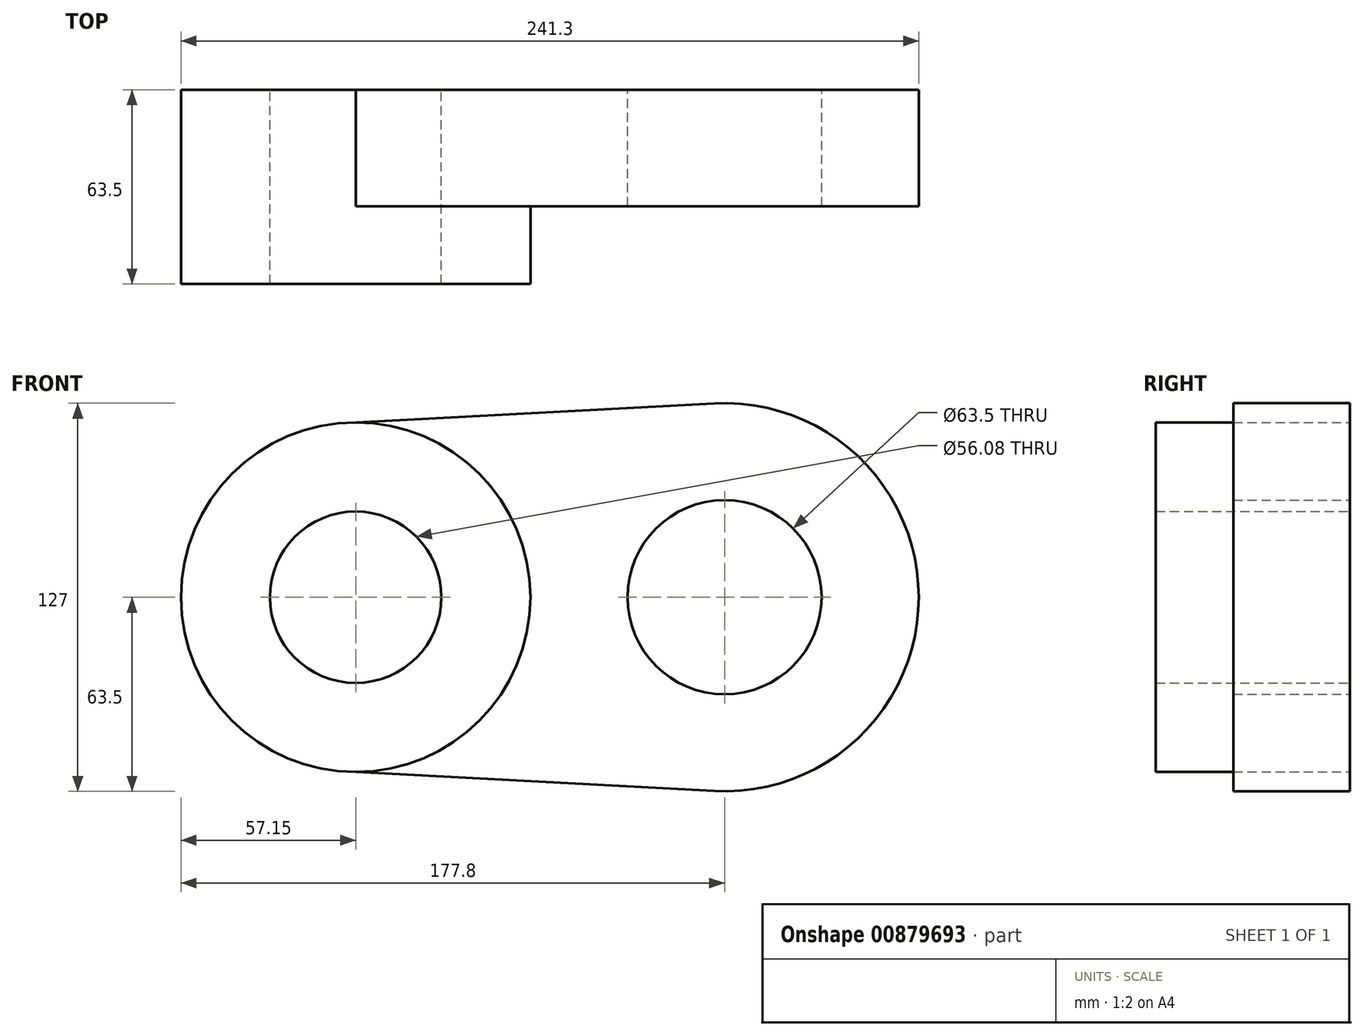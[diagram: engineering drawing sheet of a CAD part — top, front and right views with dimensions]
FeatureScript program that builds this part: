
annotation { "Feature Type Name" : "Feature", "Feature Type Description" : "" }
export const myFeature = defineFeature(function(context is Context, id is Id, definition is map)
    precondition{}
    {
        {
            var Q0;
            Q0=qCreatedBy(makeId("Front.planeOp"),FACE);
            var sketch = newSketch(context, id + "F0", { "sketchPlane" : qUnion([Q0])});
            skCircle(sketch, "E0", {"center": v(0, 0) * mm, "radius": 57.15 * mm});
            skCircle(sketch, "E1", {"center": v(120.65, 0) * mm, "radius": 63.5 * mm});
            skLineSegment(sketch, "E2", {"start": v(0, 57.15) * mm, "end": v(117.27, 63.4) * mm});
            skLineSegment(sketch, "E3", {"start": v(0, -57.15) * mm, "end": v(117.27, -63.4) * mm});
            skCircle(sketch, "E4", {"center": v(0, 0) * mm, "radius": 28.04 * mm});
            skCircle(sketch, "E5", {"center": v(120.65, 0) * mm, "radius": 31.75 * mm});
            skSolve(sketch);
        }
        {
            var Q0;
            Q0 = qSketchRegion(id + "F0", true);
            extrude(context, id + "F1", {"entities" : qUnion([Q0]), "depth" : 38.1 * mm, "offsetDistance" : 25.4 * mm});
        }
        {
            var Q0;
            Q0=makeQuery(id+"F0.imprint","IMPRINT",FACE,{"disambiguationData":[TD([[makeQuery(id+"F0.imprint","IMPRINT",EDGE,{"derivedFrom":sQuery(id+"F0.wireOp",EDGE,"E4")}),-1.0]])]});
            extrude(context, id + "F2", {"entities" : qUnion([Q0]), "operationType" : NewBodyOperationType.ADD, "depth" : 63.5 * mm, "offsetDistance" : 25.4 * mm});
        }
    });
